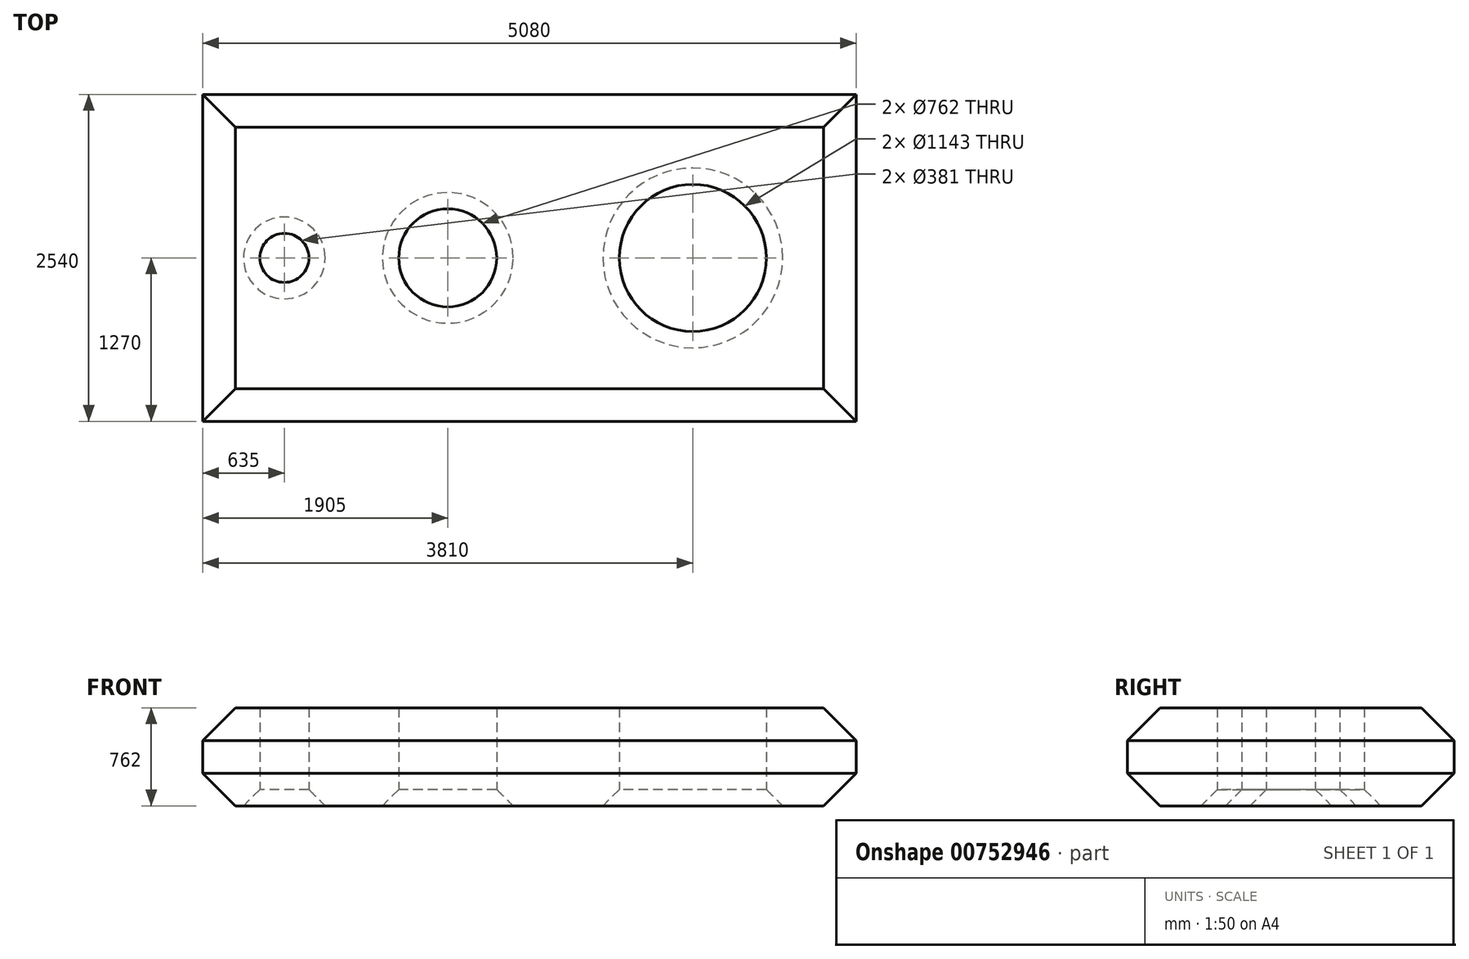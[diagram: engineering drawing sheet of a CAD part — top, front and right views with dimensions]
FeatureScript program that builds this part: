
annotation { "Feature Type Name" : "Feature", "Feature Type Description" : "" }
export const myFeature = defineFeature(function(context is Context, id is Id, definition is map)
    precondition{}
    {
        {
            var Q0;
            Q0=qCreatedBy(makeId("Top.planeOp"),FACE);
            var sketch = newSketch(context, id + "F0", { "sketchPlane" : qUnion([Q0])});
            skLineSegment(sketch, "E0.bottom", {"start": v(-3145.28, -1270) * mm, "end": v(1934.72, -1270) * mm});
            skLineSegment(sketch, "E0.top", {"start": v(-3145.28, 1270) * mm, "end": v(1934.72, 1270) * mm});
            skLineSegment(sketch, "E0.left", {"start": v(-3145.28, -1270) * mm, "end": v(-3145.28, 1270) * mm});
            skLineSegment(sketch, "E0.right", {"start": v(1934.72, -1270) * mm, "end": v(1934.72, 1270) * mm});
            skLineSegment(sketch, "E1", {"start": v(-3145.28, 0) * mm, "end": v(1934.72, 0) * mm});
            skCircle(sketch, "E2", {"center": v(-2510.28, 0) * mm, "radius": 190.5 * mm});
            skCircle(sketch, "E3", {"center": v(-1240.28, 0) * mm, "radius": 381 * mm});
            skCircle(sketch, "E4", {"center": v(664.72, 0) * mm, "radius": 571.5 * mm});
            skSolve(sketch);
        }
        {
            var Q0;
            Q0=makeQuery(id+"F0.imprint","IMPRINT",FACE,{"disambiguationData":[TD([[makeQuery(id+"F0.imprint","IMPRINT",EDGE,{"derivedFrom":sQuery(id+"F0.wireOp",EDGE,"E0.bottom")}),1.0]])]});
            var Q1;
            {var subQ1=sQuery(id+"F0.wireOp",EDGE,"E0.top");Q1=makeQuery(id+"F0.imprint","IMPRINT",FACE,{"disambiguationData":[TD([[makeQuery(id+"F0.imprint","IMPRINT",EDGE,{"derivedFrom":subQ1}),-1.0]])]});}
            extrude(context, id + "F1", {"entities" : qUnion([Q0, Q1]), "depth" : 762 * mm, "offsetDistance" : 25.4 * mm});
        }
        {
            var Q0;
            Q0=makeQuery(id+"F1.opExtrude","CAP_EDGE",EDGE,{"disambiguationData":[OSD([sQuery(id+"F0.wireOp",EDGE,"E0.left")])],"isStart":true});
            var Q1;
            Q1=makeQuery(id+"F1.opExtrude","CAP_EDGE",EDGE,{"disambiguationData":[OSD([sQuery(id+"F0.wireOp",EDGE,"E0.top")])],"isStart":true});
            var Q2;
            Q2=makeQuery(id+"F1.opExtrude","CAP_EDGE",EDGE,{"disambiguationData":[OSD([sQuery(id+"F0.wireOp",EDGE,"E0.right")])],"isStart":true});
            var Q3;
            Q3=makeQuery(id+"F1.opExtrude","CAP_EDGE",EDGE,{"disambiguationData":[OSD([sQuery(id+"F0.wireOp",EDGE,"E0.right")])],"isStart":false});
            var Q4;
            Q4=makeQuery(id+"F1.opExtrude","CAP_EDGE",EDGE,{"disambiguationData":[OSD([sQuery(id+"F0.wireOp",EDGE,"E0.bottom")])],"isStart":false});
            var Q5;
            Q5=makeQuery(id+"F1.opExtrude","CAP_EDGE",EDGE,{"disambiguationData":[OSD([sQuery(id+"F0.wireOp",EDGE,"E0.left")])],"isStart":false});
            var Q6;
            Q6=makeQuery(id+"F1.opExtrude","CAP_EDGE",EDGE,{"disambiguationData":[OSD([sQuery(id+"F0.wireOp",EDGE,"E0.top")])],"isStart":false});
            var Q7;
            Q7=makeQuery(id+"F1.opExtrude","CAP_EDGE",EDGE,{"disambiguationData":[OSD([sQuery(id+"F0.wireOp",EDGE,"E0.bottom")])],"isStart":true});
            chamfer(context, id + "F2", {"entities" : qUnion([Q0, Q1, Q2, Q3, Q4, Q5, Q6, Q7]), "width" : 254 * mm, "tangentPropagation" : true});
        }
        {
            var Q0;
            Q0=makeQuery(id+"F1.opExtrude","CAP_EDGE",EDGE,{"disambiguationData":[OSD([sQuery(id+"F0.wireOp",EDGE,"E2")])],"isStart":true});
            var Q1;
            Q1=makeQuery(id+"F1.opExtrude","CAP_EDGE",EDGE,{"disambiguationData":[OSD([sQuery(id+"F0.wireOp",EDGE,"E3")])],"isStart":true});
            var Q2;
            Q2=makeQuery(id+"F1.opExtrude","CAP_EDGE",EDGE,{"disambiguationData":[OSD([sQuery(id+"F0.wireOp",EDGE,"E4")])],"isStart":true});
            chamfer(context, id + "F3", {"entities" : qUnion([Q0, Q1, Q2]), "width" : 127 * mm, "tangentPropagation" : true});
        }
    });
